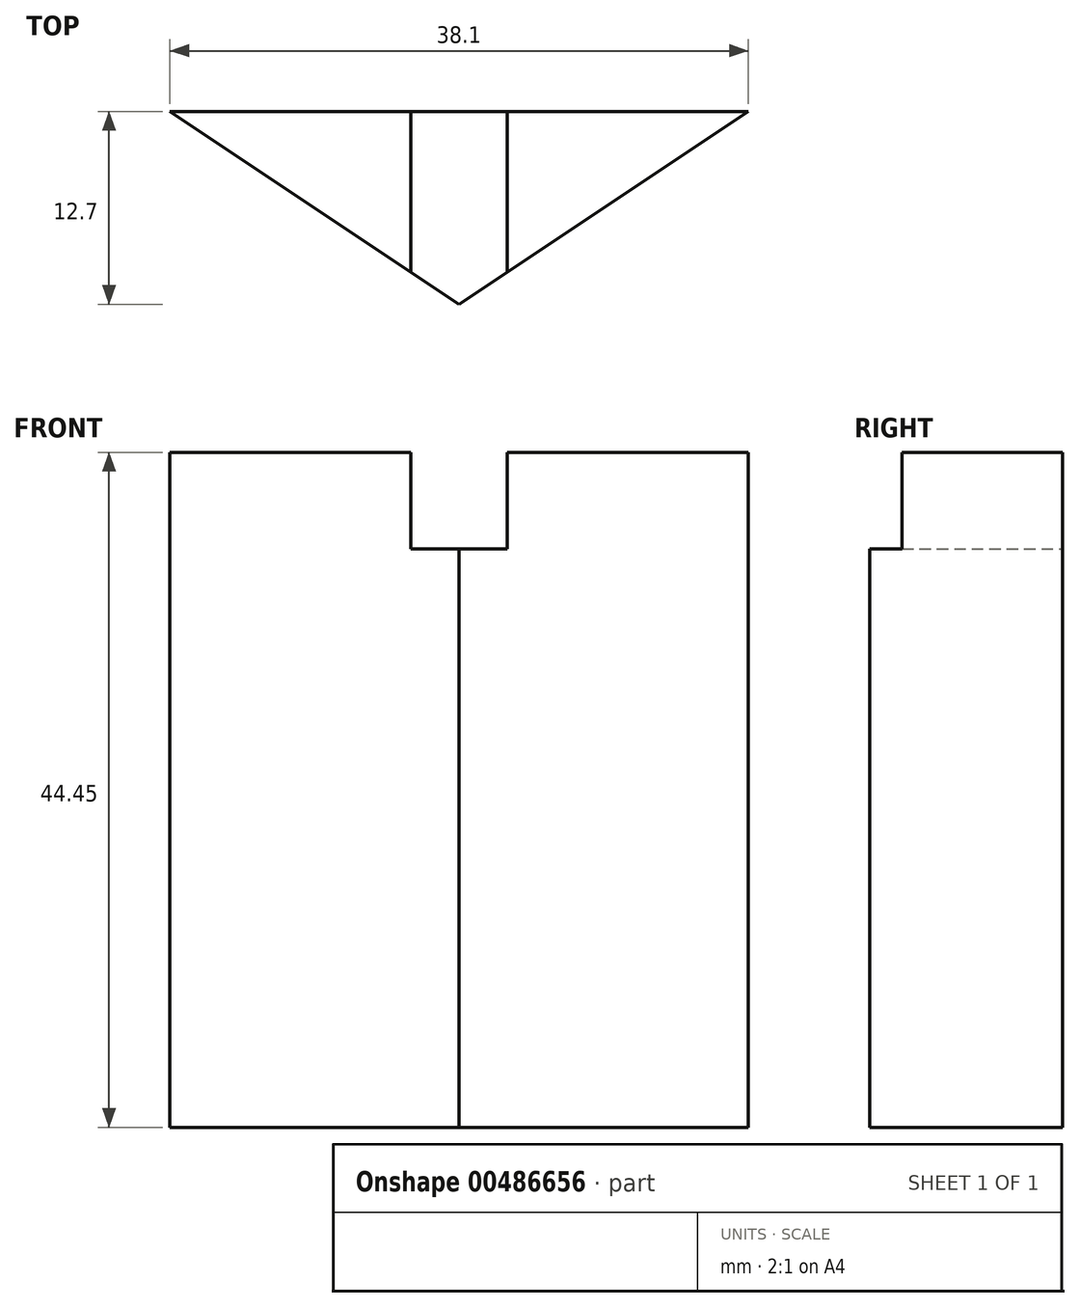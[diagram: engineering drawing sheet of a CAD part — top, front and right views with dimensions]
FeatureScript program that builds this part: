
annotation { "Feature Type Name" : "Feature", "Feature Type Description" : "" }
export const myFeature = defineFeature(function(context is Context, id is Id, definition is map)
    precondition{}
    {
        {
            var Q0;
            Q0=qCreatedBy(makeId("Top.planeOp"),FACE);
            var sketch = newSketch(context, id + "F0", { "sketchPlane" : qUnion([Q0])});
            skLineSegment(sketch, "E0", {"start": v(0, 0) * mm, "end": v(0, 12.7) * mm});
            skLineSegment(sketch, "E1", {"start": v(-19.05, 12.7) * mm, "end": v(19.05, 12.7) * mm});
            skLineSegment(sketch, "E2", {"start": v(-19.05, 12.7) * mm, "end": v(0, 0) * mm});
            skLineSegment(sketch, "E3", {"start": v(0, 0) * mm, "end": v(19.05, 12.7) * mm});
            skLineSegment(sketch, "E4.bottom", {"start": v(-12.7, 12.7) * mm, "end": v(12.7, 12.7) * mm});
            skSolve(sketch);
        }
        {
            var Q0;
            {var subQ0=sQuery(id+"F0.wireOp",EDGE,"E0");Q0=makeQuery(id+"F0.imprint","IMPRINT",FACE,{"disambiguationData":[TD([[makeQuery(id+"F0.imprint","IMPRINT",EDGE,{"derivedFrom":subQ0}),1.0]])]});}
            var Q1;
            {var subQ0=sQuery(id+"F0.wireOp",EDGE,"E0");Q1=makeQuery(id+"F0.imprint","IMPRINT",FACE,{"disambiguationData":[TD([[makeQuery(id+"F0.imprint","IMPRINT",EDGE,{"derivedFrom":subQ0}),-1.0]])]});}
            extrude(context, id + "F1", {"entities" : qUnion([Q0, Q1]), "depth" : 44.45 * mm});
        }
        {
            var Q0;
            Q0=makeQuery(id+"F1.opExtrude","SWEPT_FACE",FACE,{"disambiguationData":[OSD([sQuery(id+"F0.wireOp",EDGE,"E1"),sQuery(id+"F0.wireOp",EDGE,"E4.bottom")])]});
            var sketch = newSketch(context, id + "F2", { "sketchPlane" : qUnion([Q0])});
            skLineSegment(sketch, "E5.bottom", {"start": v(-3.18, 44.45) * mm, "end": v(3.17, 44.45) * mm});
            skLineSegment(sketch, "E5.top", {"start": v(-3.18, 38.1) * mm, "end": v(3.17, 38.1) * mm});
            skLineSegment(sketch, "E5.left", {"start": v(-3.18, 44.45) * mm, "end": v(-3.18, 38.1) * mm});
            skLineSegment(sketch, "E5.right", {"start": v(3.17, 44.45) * mm, "end": v(3.17, 38.1) * mm});
            skPoint(sketch, "E5.middle", {"position": v(0, 41.28) * mm});
            skSolve(sketch);
        }
        {
            var Q0;
            Q0 = qSketchRegion(id + "F2", true);
            extrude(context, id + "F3", {"entities" : qUnion([Q0]), "operationType" : NewBodyOperationType.REMOVE, "oppositeDirection" : true, "depth" : 25.4 * mm, "offsetDistance" : 25.4 * mm});
        }
    });
